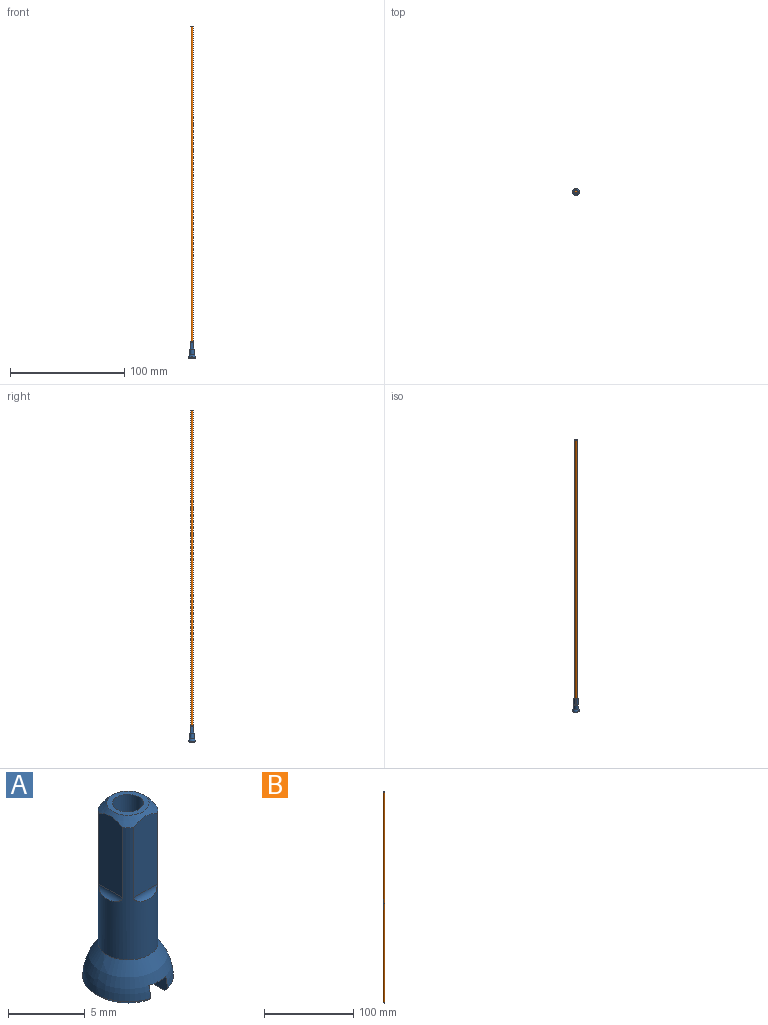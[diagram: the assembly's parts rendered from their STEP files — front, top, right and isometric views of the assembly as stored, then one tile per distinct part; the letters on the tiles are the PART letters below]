
ASSEMBLY  parts=2 mates=1
PART A: 23 faces, bbox 5.9x5.9x14.1 mm
  f0: plane 5.21x1.94mm, normal (0,0,-1), area 7.3mm2, adj f1,f15,f18,f21
  f1: cone r=2.72mm half-angle=43.4deg, axis (0,0,1), area 2.7mm2, adj f0,f9,f18,f21
  f2: plane 2.75x2.75mm, normal (0,0,1), area 2.8mm2, adj f15,f16
  f3: cylinder r=1.95mm len=10.58mm, axis (0,0,-1), area 73.3mm2, adj f4,f5,f6,f7,f9,f10,f11,f12
  f4: plane 5.97x2.21mm, normal (1,0,0), area 12.9mm2, adj f3,f12,f16
  f5: plane 5.97x2.21mm, normal (0,1,0), area 12.9mm2, adj f3,f10,f16
  f6: plane 5.97x2.21mm, normal (-1,0,0), area 12.9mm2, adj f3,f11,f16
  f7: plane 5.97x2.21mm, normal (0,-1,0), area 12.9mm2, adj f3,f13,f16
  f8: plane 5.21x1.94mm, normal (0,0,-1), area 7.3mm2, adj f14,f15,f19,f20
  f9: revolved ~5.94x5.94mm, area 43.8mm2, adj f1,f3,f14,f17,f18,f19,f20,f21
  f10: cylinder r=0.5mm len=2.2mm, axis (1,0,0), area 1.1mm2, adj f3,f5
  f11: cylinder r=0.5mm len=2.2mm, axis (0,1,0), area 1.1mm2, adj f3,f6
  f12: cylinder r=0.5mm len=2.2mm, axis (0,-1,0), area 1.1mm2, adj f3,f4
  f13: cylinder r=0.5mm len=2.2mm, axis (-1,0,0), area 1.1mm2, adj f3,f7
  f14: cone r=2.72mm half-angle=43.4deg, axis (0,0,1), area 2.7mm2, adj f8,f9,f19,f20
  f15: cylinder r=1mm len=14.05mm, axis (0,0,1), area 84mm2, adj f0,f2,f8,f17,f18,f19,f20,f21
  f16: cone r=1.38mm half-angle=45deg, axis (0,0,-1), area 5.6mm2, adj f2,f3,f4,f5,f6,f7
  f17: plane 2.18x1.55mm, normal (0,0,-1), area 2.9mm2, adj f9,f15,f18,f19
  f18: plane 2.25x1.22mm, normal (-1,0,0), area 2.6mm2, adj f0,f1,f9,f15,f17
  f19: plane 2.25x1.22mm, normal (1,0,0), area 2.6mm2, adj f8,f9,f14,f15,f17
  f20: plane 2.25x1.22mm, normal (1,0,0), area 2.6mm2, adj f8,f9,f14,f15,f22
  f21: plane 2.25x1.22mm, normal (-1,0,0), area 2.6mm2, adj f0,f1,f9,f15,f22
  f22: plane 2.18x1.55mm, normal (0,0,-1), area 2.9mm2, adj f9,f15,f20,f21
PART B: 3 faces, bbox 2x2x290 mm
  f0: cylinder r=1mm len=290mm, axis (0,0,-1), area 1822.1mm2, adj f1,f2
  f1: plane 2x2mm, normal (0,0,1), area 3.1mm2, adj f0
  f2: plane 2x2mm, normal (0,0,-1), area 3.1mm2, adj f0
PLACE A t=(-0.78,0.65,-0.06)mm fixed
PLACE B t=(-0.78,0.65,-0.06)mm
MATE fastened B.f0 <-> A.f1  axis (0,0,-1) through (-0.78,0.65,-0.06)mm
